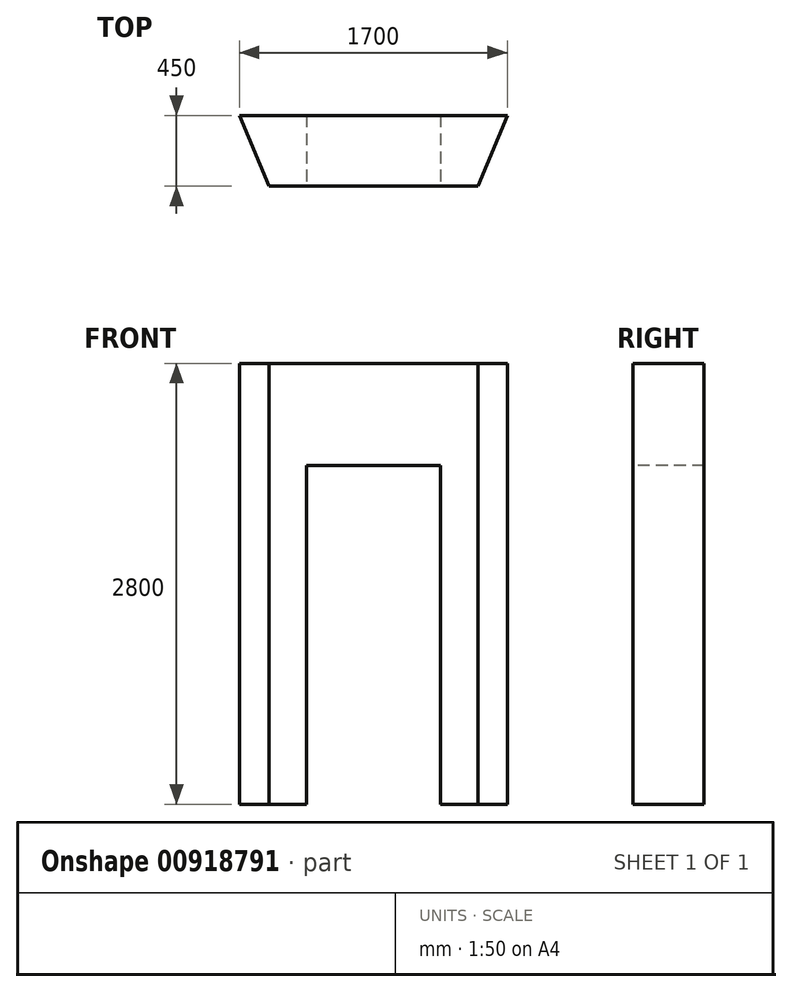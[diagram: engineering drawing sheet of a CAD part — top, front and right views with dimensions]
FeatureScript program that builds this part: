
annotation { "Feature Type Name" : "Feature", "Feature Type Description" : "" }
export const myFeature = defineFeature(function(context is Context, id is Id, definition is map)
    precondition{}
    {
        {
            var Q0;
            Q0=qCreatedBy(makeId("Top.planeOp"),FACE);
            var sketch = newSketch(context, id + "F0", { "sketchPlane" : qUnion([Q0])});
            skLineSegment(sketch, "E0", {"start": v(0, 0) * mm, "end": v(-186.4, 450) * mm});
            skLineSegment(sketch, "E1", {"start": v(-186.4, 450) * mm, "end": v(1513.6, 450) * mm});
            skLineSegment(sketch, "E2", {"start": v(1513.6, 450) * mm, "end": v(1327.2, 0) * mm});
            skLineSegment(sketch, "E3", {"start": v(1327.2, 0) * mm, "end": v(0, 0) * mm});
            skSolve(sketch);
        }
        {
            var Q0;
            Q0=makeQuery(id+"F0.imprint","IMPRINT",FACE,{"disambiguationData":[TD([[makeQuery(id+"F0.imprint","IMPRINT",EDGE,{"derivedFrom":sQuery(id+"F0.wireOp",EDGE,"E0")}),-1.0]])]});
            extrude(context, id + "F1", {"entities" : qUnion([Q0]), "depth" : 2800 * mm, "offsetDistance" : 25 * mm});
        }
        {
            var Q0;
            Q0=makeQuery(id+"F1.opExtrude","SWEPT_FACE",FACE,{"disambiguationData":[OSD([sQuery(id+"F0.wireOp",EDGE,"E3")])]});
            var sketch = newSketch(context, id + "F2", { "sketchPlane" : qUnion([Q0])});
            skLineSegment(sketch, "E4", {"start": v(238.6, 0) * mm, "end": v(238.6, 2150) * mm});
            skLineSegment(sketch, "E5", {"start": v(238.6, 2150) * mm, "end": v(1088.6, 2150) * mm});
            skLineSegment(sketch, "E6", {"start": v(1088.6, 2150) * mm, "end": v(1088.6, 0) * mm});
            skLineSegment(sketch, "E7", {"start": v(238.6, 2150) * mm, "end": v(0, 2150) * mm, "construction": true});
            skLineSegment(sketch, "E8", {"start": v(1088.6, 2150) * mm, "end": v(1327.2, 2150) * mm, "construction": true});
            skSolve(sketch);
        }
        {
            var Q0;
            {var subQ0=sQuery(id+"F2.wireOp",EDGE,"E4");Q0=makeQuery(id+"F2.imprint","IMPRINT",FACE,{"disambiguationData":[TD([[makeQuery(id+"F2.imprint","IMPRINT",EDGE,{"derivedFrom":subQ0}),-1.0]])]});}
            extrude(context, id + "F3", {"entities" : qUnion([Q0]), "operationType" : NewBodyOperationType.REMOVE, "endBound" : BoundingType.THROUGH_ALL, "oppositeDirection" : true, "depth" : 25 * mm, "offsetDistance" : 25 * mm});
        }
    });
